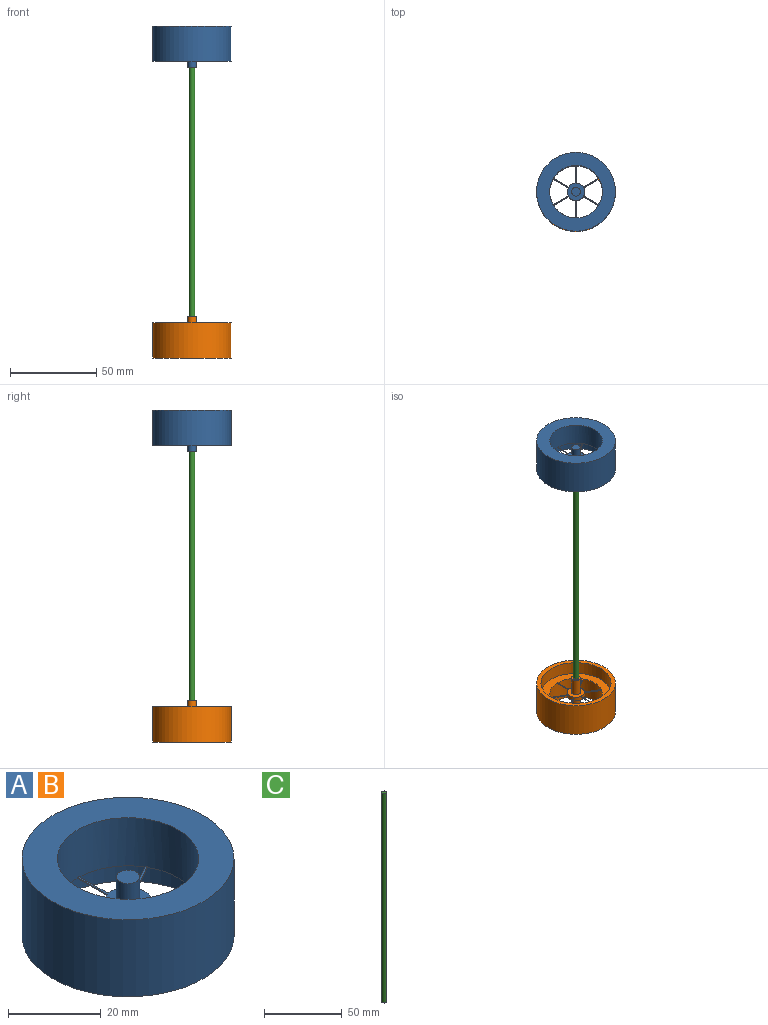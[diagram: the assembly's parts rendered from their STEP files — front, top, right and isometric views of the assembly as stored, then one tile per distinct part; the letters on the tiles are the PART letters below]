
ASSEMBLY  parts=3 mates=2
PART A: 33 faces, bbox 45.7x45.7x23.9 mm
  f0: plane 40.67x40.67mm, normal (0,0,-1), area 598.2mm2, adj f1,f11,f12,f14,f15,f17,f18,f20
  f1: cylinder r=5.08mm len=10.16mm, axis (0,0,-1), area 80.3mm2, adj f0,f2,f3,f10,f11,f12,f13,f14
  f2: plane 10.16x10.16mm, normal (0,0,1), area 60.8mm2, adj f1,f4
  f3: plane 10.16x10.16mm, normal (0,0,-1), area 60.8mm2, adj f1,f6
  f4: cylinder r=2.54mm len=6.35mm, axis (0,0,-1), area 101.3mm2, adj f2,f5
  f5: plane 5.08x5.08mm, normal (0,0,1), area 20.3mm2, adj f4
  f6: cylinder r=2.54mm len=10.16mm, axis (0,0,1), area 162.1mm2, adj f3,f7
  f7: plane 5.08x5.08mm, normal (0,0,-1), area 15.2mm2, adj f6,f8
  f8: cylinder r=1.27mm len=10.16mm, axis (0,0,-1), area 81.1mm2, adj f7,f9
  f9: plane 2.54x2.54mm, normal (0,0,-1), area 5.1mm2, adj f8
  f10: plane 10.18x0.52mm, normal (0,0,1), area 5.1mm2, adj f1,f11,f12,f29
  f11: plane 10.18x0.27mm, normal (-1,0,0), area 2.6mm2, adj f0,f1,f10,f29
  f12: plane 10.18x0.27mm, normal (1,0,0), area 2.6mm2, adj f0,f1,f10,f29
  f13: plane 9.07x5.53mm, normal (0,0,1), area 5.1mm2, adj f1,f14,f15,f29
  f14: plane 8.82x5.1mm, normal (-0.5,-0.87,0), area 2.6mm2, adj f0,f1,f13,f29
  f15: plane 8.81x5.09mm, normal (0.5,0.87,0), area 2.6mm2, adj f0,f1,f13,f29
  f16: plane 9.07x5.53mm, normal (0,0,1), area 5.1mm2, adj f1,f17,f18,f29
  f17: plane 8.82x5.1mm, normal (0.5,-0.87,0), area 2.6mm2, adj f0,f1,f16,f29
  f18: plane 8.81x5.09mm, normal (-0.5,0.87,0), area 2.6mm2, adj f0,f1,f16,f29
  f19: plane 10.18x0.52mm, normal (0,0,1), area 5.1mm2, adj f1,f20,f21,f29
  f20: plane 10.18x0.27mm, normal (1,0,0), area 2.6mm2, adj f0,f1,f19,f29
  f21: plane 10.18x0.27mm, normal (-1,0,0), area 2.6mm2, adj f0,f1,f19,f29
  f22: plane 9.07x5.53mm, normal (0,0,1), area 5.1mm2, adj f1,f23,f24,f29
  f23: plane 8.82x5.1mm, normal (0.5,0.87,0), area 2.6mm2, adj f0,f1,f22,f29
  f24: plane 8.81x5.09mm, normal (-0.5,-0.87,0), area 2.6mm2, adj f0,f1,f22,f29
  f25: plane 9.07x5.53mm, normal (0,0,1), area 5.1mm2, adj f1,f26,f27,f29
  f26: plane 8.82x5.1mm, normal (-0.5,0.87,0), area 2.6mm2, adj f0,f1,f25,f29
  f27: plane 8.81x5.09mm, normal (0.5,-0.87,0), area 2.6mm2, adj f0,f1,f25,f29
  f28: plane 45.72x45.72mm, normal (0,0,1), area 912.1mm2, adj f29,f30
  f29: cylinder r=15.24mm len=30.48mm, axis (0,0,-1), area 1215.5mm2, adj f0,f10,f11,f12,f13,f14,f15,f16
  f30: cylinder r=22.86mm len=45.72mm, axis (0,0,-1), area 2918.8mm2, adj f28,f31
  f31: plane 45.72x45.72mm, normal (0,0,-1), area 344.6mm2, adj f30,f32
  f32: cylinder r=20.32mm len=40.64mm, axis (0,0,-1), area 973mm2, adj f0,f31
PART B: same geometry as A
PART C: 3 faces, bbox 3.2x3.2x165.1 mm
  f0: cylinder r=1.59mm len=165.1mm, axis (0,0,-1), area 1646.8mm2, adj f1,f2
  f1: plane 3.18x3.18mm, normal (0,0,1), area 7.9mm2, adj f0
  f2: plane 3.18x3.18mm, normal (0,0,-1), area 7.9mm2, adj f0
PLACE A t=(0,0,180.09)mm
PLACE B rot(axis=(1,0,0),180deg) t=(0,0,12.45)mm
PLACE C rot(axis=(1,0,0),180deg) t=(0,0,178.82)mm
MATE fastened B.f1 <-> C.f0  axis (0,0,1) through (0,0,13.72)mm
MATE fastened A.f1 <-> C.f0  axis (0,0,-1) through (0,0,178.82)mm
